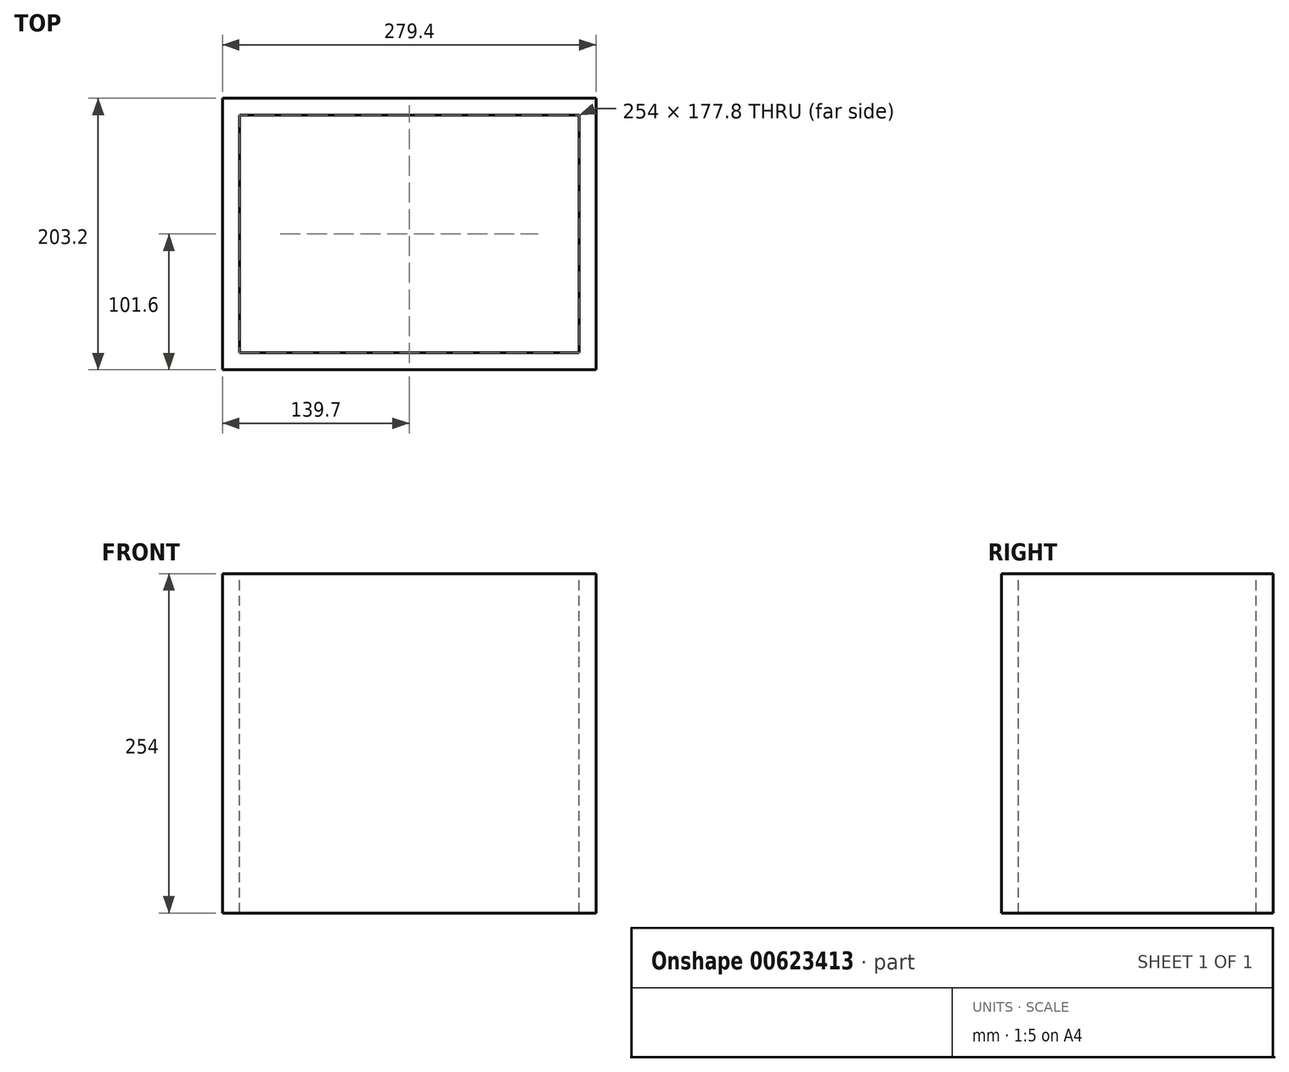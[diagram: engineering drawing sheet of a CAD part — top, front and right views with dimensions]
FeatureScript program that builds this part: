
annotation { "Feature Type Name" : "Feature", "Feature Type Description" : "" }
export const myFeature = defineFeature(function(context is Context, id is Id, definition is map)
    precondition{}
    {
        {
            var Q0;
            Q0=qCreatedBy(makeId("Front.planeOp"),FACE);
            var sketch = newSketch(context, id + "F0", { "sketchPlane" : qUnion([Q0])});
            skLineSegment(sketch, "E0", {"start": v(-59.22, 134.94) * mm, "end": v(-59.22, -119.06) * mm});
            skLineSegment(sketch, "E1", {"start": v(-59.22, -119.06) * mm, "end": v(220.18, -119.06) * mm});
            skLineSegment(sketch, "E2", {"start": v(220.18, -119.06) * mm, "end": v(220.18, 134.94) * mm});
            skLineSegment(sketch, "E3", {"start": v(220.18, 134.94) * mm, "end": v(-59.22, 134.94) * mm});
            skSolve(sketch);
        }
        {
            var Q0;
            Q0=makeQuery(id+"F0.imprint","IMPRINT",FACE,{"disambiguationData":[TD([[makeQuery(id+"F0.imprint","IMPRINT",EDGE,{"derivedFrom":sQuery(id+"F0.wireOp",EDGE,"E0")}),1.0]])]});
            extrude(context, id + "F1", {"entities" : qUnion([Q0]), "depth" : 203.2 * mm, "offsetDistance" : 25.4 * mm});
        }
        {
            var Q0;
            Q0=makeQuery(id+"F1.opExtrude","SWEPT_FACE",FACE,{"disambiguationData":[OSD([sQuery(id+"F0.wireOp",EDGE,"E3")])]});
            var sketch = newSketch(context, id + "F2", { "sketchPlane" : qUnion([Q0])});
            skLineSegment(sketch, "E4", {"start": v(80.48, -12.7) * mm, "end": v(-46.52, -12.7) * mm});
            skLineSegment(sketch, "E5", {"start": v(-46.52, -12.7) * mm, "end": v(-46.52, -101.6) * mm});
            skLineSegment(sketch, "E6", {"start": v(-46.52, -101.6) * mm, "end": v(-46.52, -190.5) * mm});
            skLineSegment(sketch, "E7", {"start": v(-46.52, -190.5) * mm, "end": v(80.48, -190.5) * mm});
            skLineSegment(sketch, "E8", {"start": v(80.48, -190.5) * mm, "end": v(207.48, -190.5) * mm});
            skLineSegment(sketch, "E9", {"start": v(207.48, -190.5) * mm, "end": v(207.48, -101.6) * mm});
            skLineSegment(sketch, "E10", {"start": v(207.48, -101.6) * mm, "end": v(207.48, -12.7) * mm});
            skLineSegment(sketch, "E11", {"start": v(207.48, -12.7) * mm, "end": v(80.48, -12.7) * mm});
            skSolve(sketch);
        }
        {
            var Q0;
            Q0=makeQuery(id+"F2.imprint","IMPRINT",FACE,{"disambiguationData":[TD([[makeQuery(id+"F2.imprint","IMPRINT",EDGE,{"derivedFrom":sQuery(id+"F2.wireOp",EDGE,"E4")}),1.0]])]});
            extrude(context, id + "F3", {"entities" : qUnion([Q0]), "operationType" : NewBodyOperationType.REMOVE, "oppositeDirection" : true, "depth" : 279.4 * mm, "offsetDistance" : 25.4 * mm});
        }
    });
